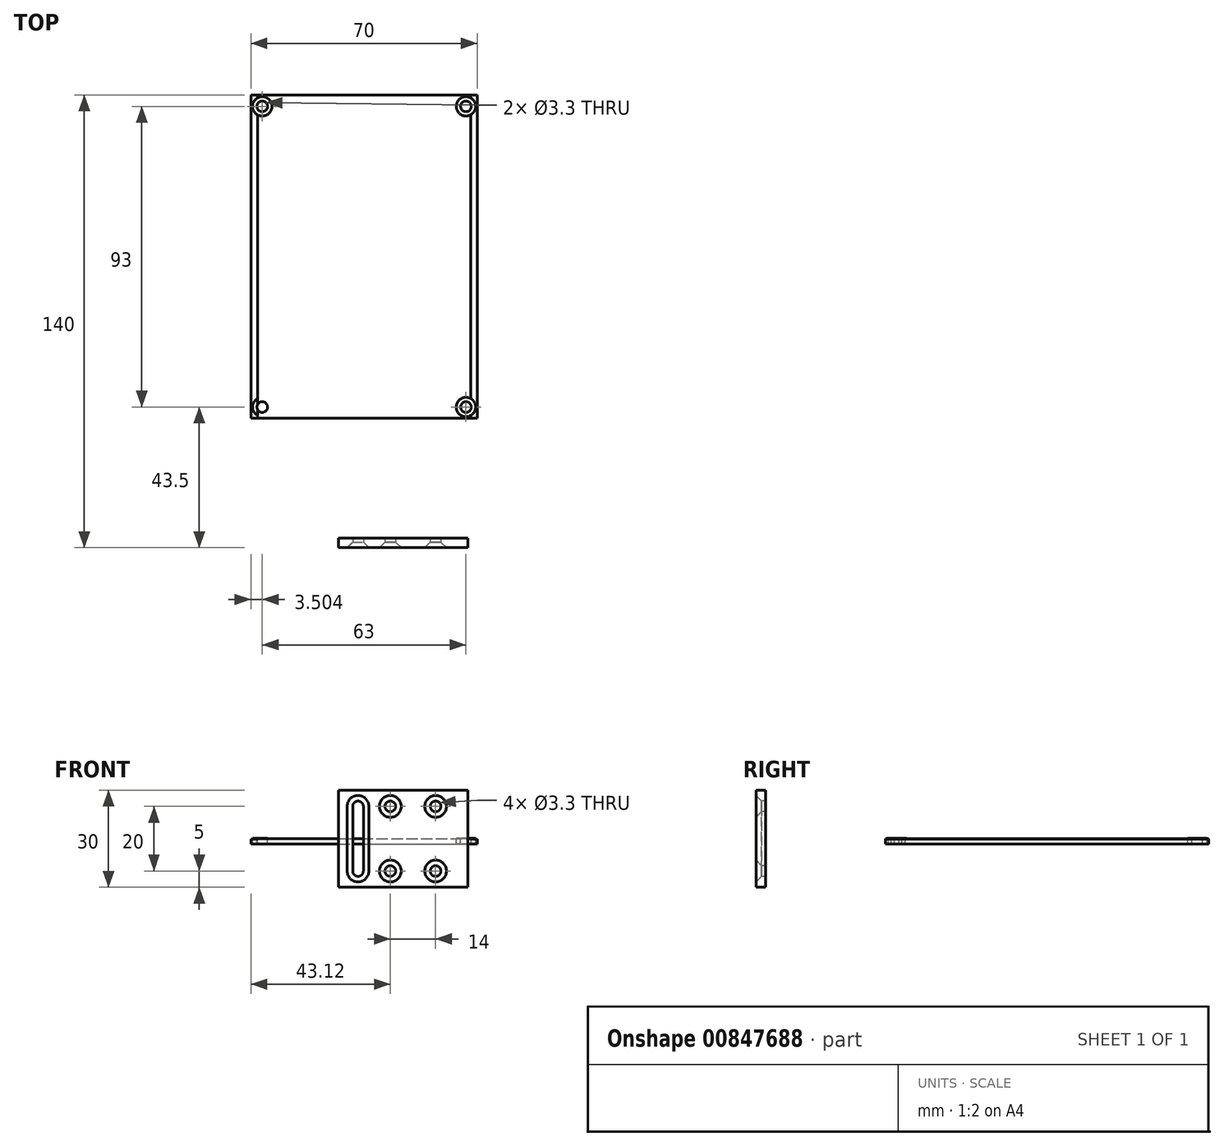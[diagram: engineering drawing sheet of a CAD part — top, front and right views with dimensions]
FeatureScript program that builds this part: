
annotation { "Feature Type Name" : "Feature", "Feature Type Description" : "" }
export const myFeature = defineFeature(function(context is Context, id is Id, definition is map)
    precondition{}
    {
        {
            var Q0;
            Q0=qCreatedBy(makeId("Front.planeOp"),FACE);
            var sketch = newSketch(context, id + "F0", { "sketchPlane" : qUnion([Q0])});
            skLineSegment(sketch, "E0.bottom", {"start": v(-10, 15) * mm, "end": v(10, 15) * mm});
            skLineSegment(sketch, "E0.top", {"start": v(-10, -15) * mm, "end": v(10, -15) * mm});
            skLineSegment(sketch, "E0.left", {"start": v(-10, 15) * mm, "end": v(-10, -15) * mm});
            skLineSegment(sketch, "E0.right", {"start": v(10, 15) * mm, "end": v(10, -15) * mm});
            skArc(sketch, "E1", {"start": v(-2.35, 10) * mm, "mid": v(-4, 11.65) * mm, "end": v(-5.65, 9.99) * mm});
            skArc(sketch, "E2", {"start": v(-5.65, -9.99) * mm, "mid": v(-4, -11.65) * mm, "end": v(-2.35, -10) * mm});
            skLineSegment(sketch, "E3", {"start": v(-5.65, 9.99) * mm, "end": v(-5.65, -10.01) * mm});
            skLineSegment(sketch, "E4", {"start": v(-2.35, 10) * mm, "end": v(-2.35, -10) * mm});
            skPoint(sketch, "E5", {"position": v(6, 10) * mm});
            skPoint(sketch, "E6", {"position": v(6, -10) * mm});
            skLineSegment(sketch, "E7.bottom", {"start": v(10, 15) * mm, "end": v(30, 15) * mm});
            skLineSegment(sketch, "E7.top", {"start": v(10, -15) * mm, "end": v(30, -15) * mm});
            skLineSegment(sketch, "E7.right", {"start": v(30, 15) * mm, "end": v(30, -15) * mm});
            skPoint(sketch, "E8", {"position": v(20, 10) * mm});
            skPoint(sketch, "E8.positionSnap0", {"position": v(20, 15) * mm});
            skPoint(sketch, "E9", {"position": v(20, -10) * mm});
            skSolve(sketch);
        }
        {
            var Q0;
            Q0 = qSketchRegion(id + "F0", true);
            var Q1;
            Q1=makeQuery(id+"F0.imprint","IMPRINT",FACE,{"disambiguationData":[TD([[makeQuery(id+"F0.imprint","IMPRINT",EDGE,{"derivedFrom":sQuery(id+"F0.wireOp",EDGE,"E0.bottom")}),-1.0]])]});
            extrude(context, id + "F1", {"entities" : qUnion([Q0, Q1]), "oppositeDirection" : true, "depth" : 3 * mm, "offsetDistance" : 25 * mm});
        }
        {
            var Q0;
            Q0=makeQuery(id+"F1.opExtrude","CAP_EDGE",EDGE,{"disambiguationData":[OSD([sQuery(id+"F0.wireOp",EDGE,"E3")])],"isStart":true});
            var Q1;
            Q1=makeQuery(id+"F1.opExtrude","CAP_EDGE",EDGE,{"disambiguationData":[OSD([sQuery(id+"F0.wireOp",EDGE,"E1")])],"isStart":true});
            chamfer(context, id + "F2", {"entities" : qUnion([Q0, Q1]), "width" : 1.71 * mm, "tangentPropagation" : true});
        }
        {
            var Q0;
            Q0=sQuery(id+"F0.wireOp",VERTEX,"E5");
            var Q1;
            Q1=sQuery(id+"F0.wireOp",VERTEX,"E6");
            var Q2;
            Q2=makeQuery(id+"F1.opExtrude","SWEPT_BODY",BODY,{"disambiguationData":[OSD([sQuery(id+"F0.wireOp",EDGE,"E0.bottom"),sQuery(id+"F0.wireOp",EDGE,"E0.top"),sQuery(id+"F0.wireOp",EDGE,"E0.left"),sQuery(id+"F0.wireOp",EDGE,"E0.right"),sQuery(id+"F0.wireOp",EDGE,"E1"),sQuery(id+"F0.wireOp",EDGE,"E2"),sQuery(id+"F0.wireOp",EDGE,"E3"),sQuery(id+"F0.wireOp",EDGE,"E4")])]});
            hole(context, id + "F3", {"style" : HoleStyle.C_SINK, "endStyle" : HoleEndStyle.THROUGH, "standardTappedOrClearance" : lookupTablePath({ "fit" : "Normal", "standard" : "ISO", "size" : "M3", "type" : "Clearance" }), "standardBlindInLast" : lookupTablePath({ "fit" : "Standard", "standard" : "ISO", "size" : "M3", "type" : "Clearance" }), "holeDiameter" : 3.3 * mm, "cSinkDiameter" : 6.72 * mm, "cSinkAngle" : 90 * degree, "majorDiameter" : 3 * mm, "tappedDepth" : 4.5 * mm, "tapClearance" : 3, "startFromSketch" : true, "locations" : qUnion([Q0, Q1]), "scope" : qUnion([Q2])});
        }
        {
            var Q0;
            Q0=qCreatedBy(makeId("Top.planeOp"),FACE);
            var sketch = newSketch(context, id + "F4", { "sketchPlane" : qUnion([Q0])});
            skLineSegment(sketch, "E10.bottom", {"start": v(-37.12, 140) * mm, "end": v(32.88, 140) * mm});
            skLineSegment(sketch, "E10.top", {"start": v(-37.12, 40) * mm, "end": v(32.88, 40) * mm});
            skLineSegment(sketch, "E10.left", {"start": v(-37.12, 140) * mm, "end": v(-37.12, 40) * mm});
            skLineSegment(sketch, "E10.right", {"start": v(32.88, 140) * mm, "end": v(32.88, 40) * mm});
            skLineSegment(sketch, "E11", {"start": v(-35.12, 140) * mm, "end": v(-35.12, 40) * mm});
            skCircle(sketch, "E12", {"center": v(-33.62, 136.5) * mm, "radius": 3 * mm});
            skCircle(sketch, "E13", {"center": v(-33.62, 136.5) * mm, "radius": 1.65 * mm});
            skLineSegment(sketch, "E14", {"start": v(30.88, 140) * mm, "end": v(30.88, 40) * mm});
            skLineSegment(sketch, "E15", {"start": v(-2.12, 140) * mm, "end": v(-2.12, 40) * mm, "construction": true});
            skLineSegment(sketch, "E16", {"start": v(-35.12, 90) * mm, "end": v(30.88, 90) * mm, "construction": true});
            skCircle(sketch, "E17.MirrorC", {"center": v(29.38, 136.5) * mm, "radius": 1.65 * mm});
            skCircle(sketch, "E18.MirrorC", {"center": v(29.38, 136.5) * mm, "radius": 3 * mm});
            skCircle(sketch, "E19.MirrorC", {"center": v(-33.62, 43.5) * mm, "radius": 1.65 * mm});
            skCircle(sketch, "E20.MirrorC", {"center": v(-33.62, 43.5) * mm, "radius": 3 * mm});
            skCircle(sketch, "E21.MirrorC", {"center": v(29.38, 43.5) * mm, "radius": 1.65 * mm});
            skCircle(sketch, "E22.MirrorC", {"center": v(29.38, 43.5) * mm, "radius": 3 * mm});
            skSolve(sketch);
        }
        {
            var Q0;
            {var subQ0=sQuery(id+"F4.wireOp",EDGE,"E11");Q0=makeQuery(id+"F4.imprint","IMPRINT",FACE,{"disambiguationData":[TD([[makeQuery(id+"F4.imprint","IMPRINT",EDGE,{"derivedFrom":subQ0}),1.0]])]});}
            var Q1;
            Q1=makeQuery(id+"F4.imprint","IMPRINT",FACE,{"disambiguationData":[TD([[makeQuery(id+"F4.imprint","IMPRINT",EDGE,{"derivedFrom":sQuery(id+"F4.wireOp",EDGE,"E12")}),1.0]])]});
            var Q2;
            Q2=makeQuery(id+"F4.imprint","IMPRINT",FACE,{"disambiguationData":[TD([[makeQuery(id+"F4.imprint","IMPRINT",EDGE,{"derivedFrom":sQuery(id+"F4.wireOp",EDGE,"E19.MirrorC")}),1.0]])]});
            var Q3;
            Q3=makeQuery(id+"F4.imprint","IMPRINT",FACE,{"disambiguationData":[TD([[makeQuery(id+"F4.imprint","IMPRINT",EDGE,{"derivedFrom":sQuery(id+"F4.wireOp",EDGE,"E17.MirrorC")}),1.0]])]});
            var Q4;
            Q4=makeQuery(id+"F4.imprint","IMPRINT",FACE,{"disambiguationData":[TD([[makeQuery(id+"F4.imprint","IMPRINT",EDGE,{"derivedFrom":sQuery(id+"F4.wireOp",EDGE,"E21.MirrorC")}),-1.0]])]});
            var Q5;
            {var subQ0=sQuery(id+"F4.wireOp",EDGE,"E10.right");Q5=makeQuery(id+"F4.imprint","IMPRINT",FACE,{"disambiguationData":[TD([[makeQuery(id+"F4.imprint","IMPRINT",EDGE,{"derivedFrom":subQ0}),-1.0]])]});}
            var Q6;
            {var subQ0=sQuery(id+"F4.wireOp",EDGE,"E10.left");Q6=makeQuery(id+"F4.imprint","IMPRINT",FACE,{"disambiguationData":[TD([[makeQuery(id+"F4.imprint","IMPRINT",EDGE,{"derivedFrom":subQ0}),1.0]])]});}
            var Q7;
            {var subQ6=sQuery(id+"F4.wireOp",EDGE,"E10.bottom");var subQ12=sQuery(id+"F4.wireOp",EDGE,"E11");var subQ18=makeQuery(id+"F4.imprint","INTERSECT",VERTEX,{"derivedFrom":[subQ6,subQ12]});Q7=makeQuery(id+"F4.imprint","IMPRINT",FACE,{"disambiguationData":[TD([[makeQuery(id+"F4.imprint","IMPRINT",EDGE,{"disambiguationData":[TD([[subQ18,-1.0]])],"derivedFrom":subQ6}),-1.0]])]});}
            extrude(context, id + "F5", {"entities" : qUnion([Q0, Q1, Q2, Q3, Q4, Q5, Q6, Q7]), "oppositeDirection" : true, "depth" : 1.6 * mm, "offsetDistance" : 25 * mm});
        }
        {
            var Q0;
            Q0=makeQuery(id+"F4.imprint","IMPRINT",FACE,{"disambiguationData":[TD([[makeQuery(id+"F4.imprint","IMPRINT",EDGE,{"derivedFrom":sQuery(id+"F4.wireOp",EDGE,"E12")}),1.0]])]});
            var Q1;
            Q1=makeQuery(id+"F4.imprint","IMPRINT",FACE,{"disambiguationData":[TD([[makeQuery(id+"F4.imprint","IMPRINT",EDGE,{"derivedFrom":sQuery(id+"F4.wireOp",EDGE,"E17.MirrorC")}),1.0]])]});
            var Q2;
            Q2=makeQuery(id+"F4.imprint","IMPRINT",FACE,{"disambiguationData":[TD([[makeQuery(id+"F4.imprint","IMPRINT",EDGE,{"derivedFrom":sQuery(id+"F4.wireOp",EDGE,"E21.MirrorC")}),-1.0]])]});
            var Q3;
            Q3=makeQuery(id+"F4.imprint","IMPRINT",FACE,{"disambiguationData":[TD([[makeQuery(id+"F4.imprint","IMPRINT",EDGE,{"derivedFrom":sQuery(id+"F4.wireOp",EDGE,"E19.MirrorC")}),1.0]])]});
            extrude(context, id + "F6", {"entities" : qUnion([Q0, Q1, Q2, Q3]), "operationType" : NewBodyOperationType.ADD, "depth" : 0.1 * mm, "offsetDistance" : 25 * mm});
        }
        {
            var Q0;
            {var subQ0=sQuery(id+"F4.wireOp",EDGE,"E10.right");Q0=makeQuery(id+"F4.imprint","IMPRINT",FACE,{"disambiguationData":[TD([[makeQuery(id+"F4.imprint","IMPRINT",EDGE,{"derivedFrom":subQ0}),-1.0]])]});}
            var Q1;
            {var subQ0=sQuery(id+"F4.wireOp",EDGE,"E10.left");Q1=makeQuery(id+"F4.imprint","IMPRINT",FACE,{"disambiguationData":[TD([[makeQuery(id+"F4.imprint","IMPRINT",EDGE,{"derivedFrom":subQ0}),1.0]])]});}
            extrude(context, id + "F7", {"entities" : qUnion([Q0, Q1]), "operationType" : NewBodyOperationType.REMOVE, "oppositeDirection" : true, "depth" : 0.1 * mm, "offsetDistance" : 25 * mm});
        }
        {
            var Q0;
            Q0=sQuery(id+"F0.wireOp",VERTEX,"E8");
            var Q1;
            Q1=sQuery(id+"F0.wireOp",VERTEX,"E9");
            var Q2;
            Q2=makeQuery(id+"F1.opExtrude","SWEPT_BODY",BODY,{"disambiguationData":[OSD([sQuery(id+"F0.wireOp",EDGE,"E0.bottom"),sQuery(id+"F0.wireOp",EDGE,"E0.top"),sQuery(id+"F0.wireOp",EDGE,"E0.left"),sQuery(id+"F0.wireOp",EDGE,"E1"),sQuery(id+"F0.wireOp",EDGE,"E2"),sQuery(id+"F0.wireOp",EDGE,"E3"),sQuery(id+"F0.wireOp",EDGE,"E4"),sQuery(id+"F0.wireOp",EDGE,"E7.bottom"),sQuery(id+"F0.wireOp",EDGE,"E7.top"),sQuery(id+"F0.wireOp",EDGE,"E7.right")])]});
            hole(context, id + "F8", {"style" : HoleStyle.C_SINK, "endStyle" : HoleEndStyle.THROUGH, "standardTappedOrClearance" : lookupTablePath({ "fit" : "Normal", "standard" : "ISO", "size" : "M3", "type" : "Clearance" }), "standardBlindInLast" : lookupTablePath({ "fit" : "Standard", "standard" : "ISO", "size" : "M3", "type" : "Clearance" }), "holeDiameter" : 3.3 * mm, "cSinkDiameter" : 6.72 * mm, "cSinkAngle" : 90 * degree, "majorDiameter" : 5 * mm, "tappedDepth" : 4.5 * mm, "tapClearance" : 3, "startFromSketch" : true, "locations" : qUnion([Q0, Q1]), "scope" : qUnion([Q2])});
        }
    });
